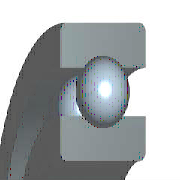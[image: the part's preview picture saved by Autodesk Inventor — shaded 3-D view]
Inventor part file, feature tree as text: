
AUTODESK INVENTOR PART (.ipt)
format: ipt  version: 2019 (Build 230136000, 136)  size: 352,768 bytes
history: native  units: mm (DEFAULTED — no unit token found)
features: other x3, plane x2, pattern_circular x1, sketch x1
ambient origin geometry x8: Origin, YZ Plane, XZ Plane, XY Plane, X Axis, Y Axis, Z Axis, Center Point
bodies: Solid1 (feature_tree)
feature tree (7):
  other  "WorkPoint1"
  other  "WorkAxis1"
  plane  "WorkPlane3"
  plane  "WorkPlane4"
  other  "WorkPoint2"
  pattern_circular  "Matriz polar1"  Count=2  [1 undecoded]
  sketch  "Boceto5"  dims[d1=10.0mm d2=72.0mm d3=26.0mm d4=19.0mm d5=8.0mm d6=360.0deg d7=0.0mm d8=15.6mm d9=4.8mm d10=360.0deg d11=-8.0mm d12=0.0mm d13=0.0mm d14=15.6001mm d15=4.8001mm d16=360.0deg d17=60.25mm d19=360.0deg d20=0.3mm d21=7.56mm d22=9.0mm d23=10.44mm d26=0.0mm d27=0.0mm d28=0.0mm d29=0.0mm d30=0.0mm]
note: 1 required parameter value undecoded (feature->parameter linkage not recoverable at this tier; creation-order binding heuristic only, values carry confidence <= 0.55)
